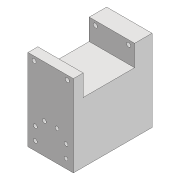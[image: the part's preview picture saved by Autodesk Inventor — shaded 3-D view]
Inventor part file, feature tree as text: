
AUTODESK INVENTOR PART (.ipt)
format: ipt  version: 2020 (Build 240168000, 168)  size: 181,760 bytes
history: native  units: mm
features: other x7, sketch x4, extrude x4, reference x4
ambient origin geometry x8: Origin, YZ Plane, XZ Plane, XY Plane, X Axis, Y Axis, Z Axis, Center Point
bodies: Body1 (feature_tree), Body2 (feature_tree)
feature tree (19):
  other  "솔리드1"
  sketch  "스케치1"
  other  "작업 평면1"
  extrude  "돌출1"  Depth=20.0mm
  sketch  "스케치2"
  other  "작업 평면2"
  extrude  "돌출2"  Depth=40.0mm
  extrude  "돌출3"  Depth=10.0mm TaperAngle=0.0deg
  extrude  "돌출4"  Depth=30.0mm
  reference  "참조1"
  reference  "참조2"
  reference  "참조3"
  sketch  "스케치3"
  sketch  "스케치4"
  reference  "참조4"
  parser-record x1  (decoder bookkeeping rows leaked as tree rows — omitted from the tree; the rows remain in map.json)
  other  "robotarm.iam"
  other  "bar2:1"
  other  "RX64_N:1"
note: 1 file-system path scrubbed to <path> (originals preserved in map.json)
